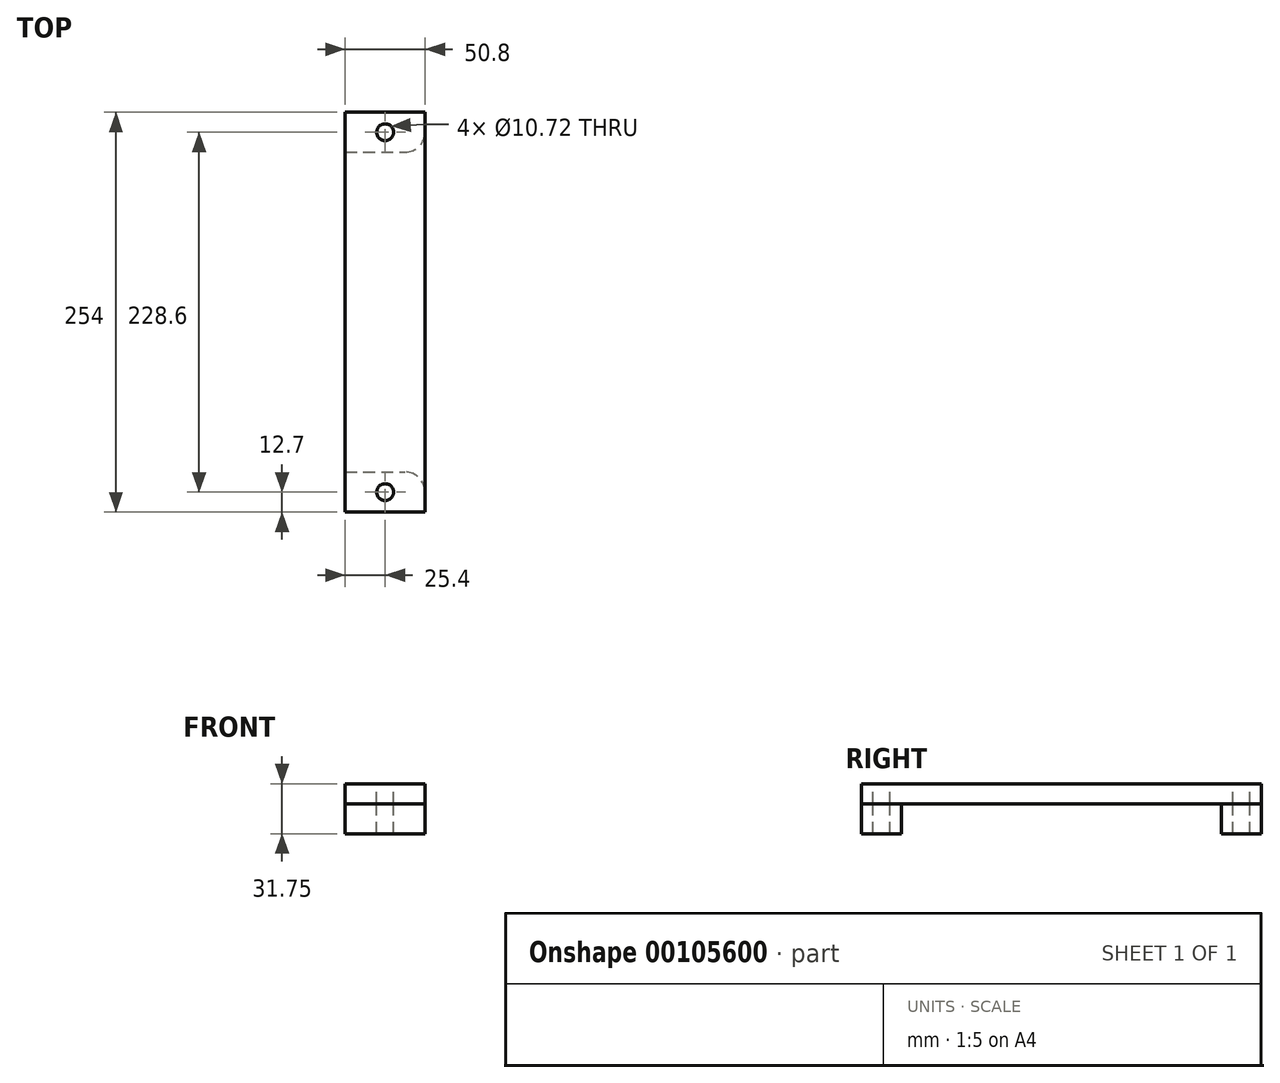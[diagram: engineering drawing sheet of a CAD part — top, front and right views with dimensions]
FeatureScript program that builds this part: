
annotation { "Feature Type Name" : "Feature", "Feature Type Description" : "" }
export const myFeature = defineFeature(function(context is Context, id is Id, definition is map)
    precondition{}
    {
        {
            var Q0;
            Q0=qCreatedBy(makeId("Top.planeOp"),FACE);
            var sketch = newSketch(context, id + "F0", { "sketchPlane" : qUnion([Q0])});
            skLineSegment(sketch, "E0.bottom", {"start": v(-25.4, 127) * mm, "end": v(25.4, 127) * mm});
            skLineSegment(sketch, "E0.top", {"start": v(-25.4, -127) * mm, "end": v(25.4, -127) * mm});
            skLineSegment(sketch, "E0.left", {"start": v(-25.4, 127) * mm, "end": v(-25.4, -127) * mm});
            skLineSegment(sketch, "E0.right", {"start": v(25.4, 127) * mm, "end": v(25.4, -127) * mm});
            skPoint(sketch, "E0.middle", {"position": v(0, 0) * mm});
            skLineSegment(sketch, "E1", {"start": v(-25.4, 101.6) * mm, "end": v(25.4, 101.6) * mm});
            skLineSegment(sketch, "E2", {"start": v(-25.4, -101.6) * mm, "end": v(25.4, -101.6) * mm});
            skSolve(sketch);
        }
        {
            var Q0;
            {var subQ0=sQuery(id+"F0.wireOp",EDGE,"E0.bottom");Q0=makeQuery(id+"F0.imprint","IMPRINT",FACE,{"disambiguationData":[TD([[makeQuery(id+"F0.imprint","IMPRINT",EDGE,{"derivedFrom":subQ0}),-1.0]])]});}
            var Q1;
            {var subQ0=sQuery(id+"F0.wireOp",EDGE,"E0.top");Q1=makeQuery(id+"F0.imprint","IMPRINT",FACE,{"disambiguationData":[TD([[makeQuery(id+"F0.imprint","IMPRINT",EDGE,{"derivedFrom":subQ0}),1.0]])]});}
            extrude(context, id + "F1", {"entities" : qUnion([Q0, Q1]), "oppositeDirection" : true, "depth" : 31.75 * mm, "hasSecondDirection" : true, "secondDirectionOppositeDirection" : true, "secondDirectionDepth" : 12.7 * mm});
        }
        {
            var Q0;
            {var subQ0=sQuery(id+"F0.wireOp",EDGE,"E1");Q0=makeQuery(id+"F0.imprint","IMPRINT",FACE,{"disambiguationData":[TD([[makeQuery(id+"F0.imprint","IMPRINT",EDGE,{"derivedFrom":subQ0}),-1.0]])]});}
            var Q1;
            {var subQ0=sQuery(id+"F0.wireOp",EDGE,"E0.bottom");Q1=makeQuery(id+"F0.imprint","IMPRINT",FACE,{"disambiguationData":[TD([[makeQuery(id+"F0.imprint","IMPRINT",EDGE,{"derivedFrom":subQ0}),-1.0]])]});}
            var Q2;
            {var subQ0=sQuery(id+"F0.wireOp",EDGE,"E0.top");Q2=makeQuery(id+"F0.imprint","IMPRINT",FACE,{"disambiguationData":[TD([[makeQuery(id+"F0.imprint","IMPRINT",EDGE,{"derivedFrom":subQ0}),1.0]])]});}
            extrude(context, id + "F2", {"entities" : qUnion([Q0, Q1, Q2]), "oppositeDirection" : true, "depth" : 12.7 * mm});
        }
        {
            var Q0;
            Q0=makeQuery(id+"F2.opExtrude","CAP_FACE",FACE,{"disambiguationData":[OSD([sQuery(id+"F0.wireOp",EDGE,"E0.bottom"),sQuery(id+"F0.wireOp",EDGE,"E0.top"),sQuery(id+"F0.wireOp",EDGE,"E0.left"),sQuery(id+"F0.wireOp",EDGE,"E0.right")])],"isStart":true});
            var sketch = newSketch(context, id + "F3", { "sketchPlane" : qUnion([Q0])});
            skPoint(sketch, "E3", {"position": v(0, 127) * mm});
            skPoint(sketch, "E4", {"position": v(0, 114.3) * mm});
            skPoint(sketch, "E5", {"position": v(0, -114.3) * mm});
            skSolve(sketch);
        }
        {
            var Q0;
            Q0=makeQuery(id+"F1.opExtrude","SWEPT_EDGE",EDGE,{"disambiguationData":[OSD([sQuery(id+"F0.wireOp",EDGE,"E0.right"),sQuery(id+"F0.wireOp",EDGE,"E2")])]});
            var Q1;
            Q1=makeQuery(id+"F1.opExtrude","SWEPT_EDGE",EDGE,{"disambiguationData":[OSD([sQuery(id+"F0.wireOp",EDGE,"E0.right"),sQuery(id+"F0.wireOp",EDGE,"E1")])]});
            fillet(context, id + "F4", {"entities" : qUnion([Q0, Q1]), "radius" : 12.7 * mm, "tangentPropagation" : true, "allowEdgeOverflow" : false});
        }
        {
            var Q0;
            Q0=sQuery(id+"F3.wireOp",VERTEX,"E4");
            var Q1;
            Q1=sQuery(id+"F3.wireOp",VERTEX,"E5");
            var Q2;
            Q2=makeQuery(id+"F2.opExtrude","SWEPT_BODY",BODY,{"disambiguationData":[OSD([sQuery(id+"F0.wireOp",EDGE,"E0.bottom"),sQuery(id+"F0.wireOp",EDGE,"E0.top"),sQuery(id+"F0.wireOp",EDGE,"E0.left"),sQuery(id+"F0.wireOp",EDGE,"E0.right")])]});
            var Q3;
            Q3=makeQuery(id+"F1.opExtrude","SWEPT_BODY",BODY,{"disambiguationData":[OSD([sQuery(id+"F0.wireOp",EDGE,"E0.bottom"),sQuery(id+"F0.wireOp",EDGE,"E0.left"),sQuery(id+"F0.wireOp",EDGE,"E0.right"),sQuery(id+"F0.wireOp",EDGE,"E1")])]});
            var Q4;
            Q4=makeQuery(id+"F1.opExtrude","SWEPT_BODY",BODY,{"disambiguationData":[OSD([sQuery(id+"F0.wireOp",EDGE,"E0.top"),sQuery(id+"F0.wireOp",EDGE,"E0.left"),sQuery(id+"F0.wireOp",EDGE,"E0.right"),sQuery(id+"F0.wireOp",EDGE,"E2")])]});
            hole(context, id + "F5", {"style" : HoleStyle.SIMPLE, "endStyle" : HoleEndStyle.THROUGH, "holeDiameter" : 10.72 * mm, "startFromSketch" : true, "locations" : qUnion([Q0, Q1]), "scope" : qUnion([Q2, Q3, Q4]), "isTappedThrough" : true});
        }
    });
